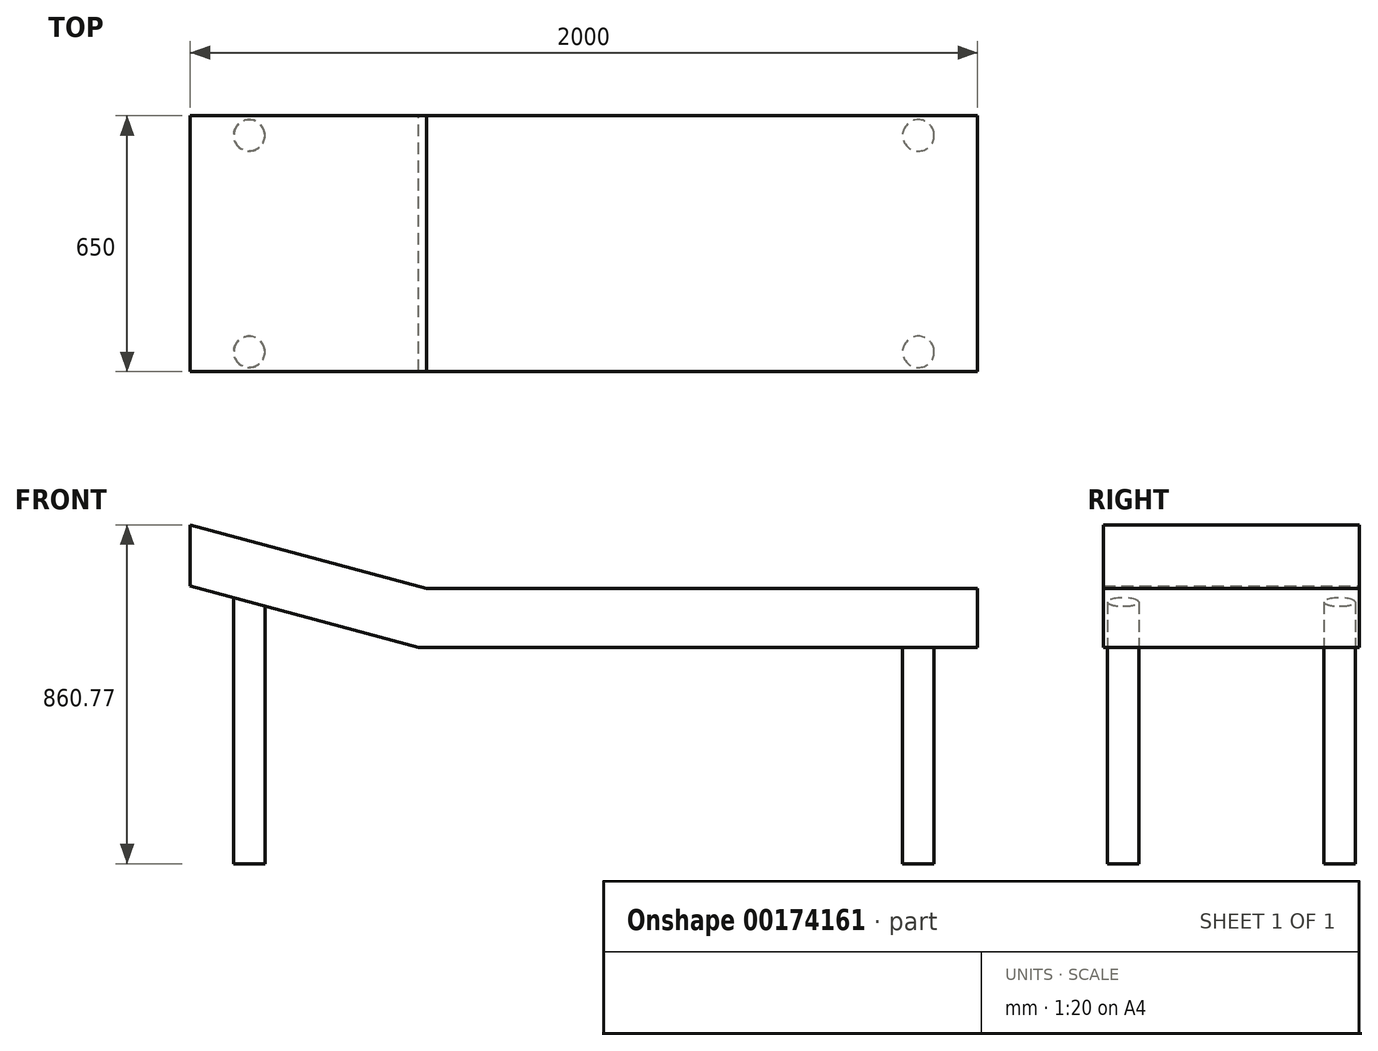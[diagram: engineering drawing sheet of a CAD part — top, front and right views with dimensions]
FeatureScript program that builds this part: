
annotation { "Feature Type Name" : "Feature", "Feature Type Description" : "" }
export const myFeature = defineFeature(function(context is Context, id is Id, definition is map)
    precondition{}
    {
        {
            var Q0;
            Q0=qCreatedBy(makeId("Top.planeOp"),FACE);
            var sketch = newSketch(context, id + "F0", { "sketchPlane" : qUnion([Q0])});
            skLineSegment(sketch, "E0", {"start": v(-850, -275) * mm, "end": v(850, 275) * mm, "construction": true});
            skLineSegment(sketch, "E1", {"start": v(-850, 275) * mm, "end": v(850, -275) * mm, "construction": true});
            skPoint(sketch, "E2", {"position": v(0, 0) * mm});
            skCircle(sketch, "E3", {"center": v(-850, 275) * mm, "radius": 40 * mm});
            skCircle(sketch, "E4", {"center": v(-850, -275) * mm, "radius": 40 * mm});
            skCircle(sketch, "E5", {"center": v(850, 275) * mm, "radius": 40 * mm});
            skCircle(sketch, "E6", {"center": v(850, -275) * mm, "radius": 40 * mm});
            skSolve(sketch);
        }
        {
            var Q0;
            Q0=makeQuery(id+"F0.imprint","IMPRINT",FACE,{"disambiguationData":[TD([[makeQuery(id+"F0.imprint","IMPRINT",EDGE,{"derivedFrom":sQuery(id+"F0.wireOp",EDGE,"E3")}),1.0]])]});
            var Q1;
            Q1=makeQuery(id+"F0.imprint","IMPRINT",FACE,{"disambiguationData":[TD([[makeQuery(id+"F0.imprint","IMPRINT",EDGE,{"derivedFrom":sQuery(id+"F0.wireOp",EDGE,"E4")}),1.0]])]});
            var Q2;
            Q2=makeQuery(id+"F0.imprint","IMPRINT",FACE,{"disambiguationData":[TD([[makeQuery(id+"F0.imprint","IMPRINT",EDGE,{"derivedFrom":sQuery(id+"F0.wireOp",EDGE,"E6")}),1.0]])]});
            var Q3;
            Q3=makeQuery(id+"F0.imprint","IMPRINT",FACE,{"disambiguationData":[TD([[makeQuery(id+"F0.imprint","IMPRINT",EDGE,{"derivedFrom":sQuery(id+"F0.wireOp",EDGE,"E5")}),1.0]])]});
            extrude(context, id + "F1", {"entities" : qUnion([Q0, Q1, Q2, Q3]), "depth" : 700 * mm});
        }
        {
            var Q0;
            Q0=qCreatedBy(makeId("Front.planeOp"),FACE);
            var sketch = newSketch(context, id + "F2", { "sketchPlane" : qUnion([Q0])});
            skLineSegment(sketch, "E7.bottom", {"start": v(-400, 700) * mm, "end": v(1000, 700) * mm});
            skLineSegment(sketch, "E7.top", {"start": v(-419.75, 550) * mm, "end": v(1000, 550) * mm});
            skLineSegment(sketch, "E7.right", {"start": v(1000, 700) * mm, "end": v(1000, 550) * mm});
            skLineSegment(sketch, "E8", {"start": v(-400, 700) * mm, "end": v(-1000, 860.77) * mm});
            skLineSegment(sketch, "E9", {"start": v(-1000, 860.77) * mm, "end": v(-1000, 705.48) * mm});
            skLineSegment(sketch, "E10", {"start": v(-1000, 705.48) * mm, "end": v(-419.75, 550) * mm});
            skSolve(sketch);
        }
        {
            var Q0;
            Q0=makeQuery(id+"F2.imprint","IMPRINT",FACE,{"disambiguationData":[TD([[makeQuery(id+"F2.imprint","IMPRINT",EDGE,{"derivedFrom":sQuery(id+"F2.wireOp",EDGE,"E7.bottom")}),-1.0]])]});
            extrude(context, id + "F3", {"entities" : qUnion([Q0]), "operationType" : NewBodyOperationType.ADD, "endBound" : BoundingType.SYMMETRIC, "depth" : 650 * mm});
        }
    });
